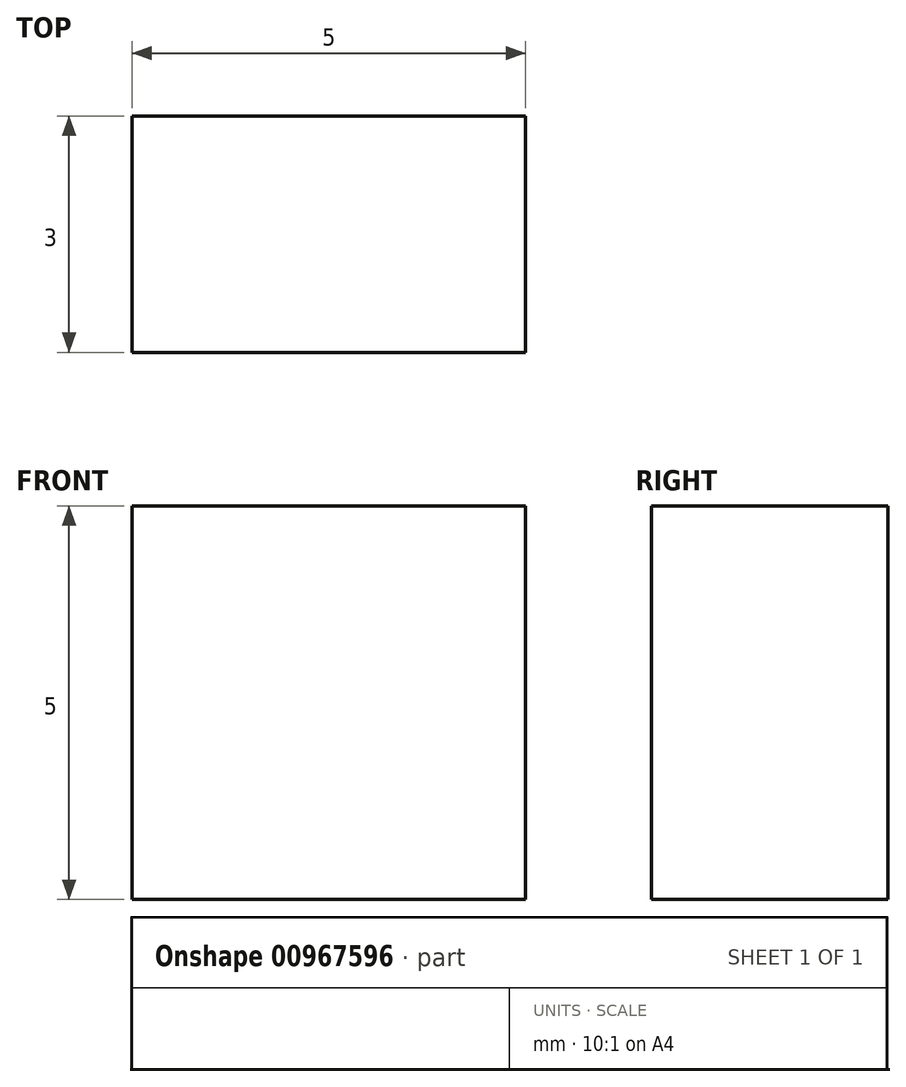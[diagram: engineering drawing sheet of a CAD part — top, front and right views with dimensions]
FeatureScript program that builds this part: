
annotation { "Feature Type Name" : "Feature", "Feature Type Description" : "" }
export const myFeature = defineFeature(function(context is Context, id is Id, definition is map)
    precondition{}
    {
        {
            var Q0;
            Q0=qCreatedBy(makeId("Front.planeOp"),FACE);
            var sketch = newSketch(context, id + "F0", { "sketchPlane" : qUnion([Q0])});
            skLineSegment(sketch, "E0.bottom", {"start": v(37.5, -50) * mm, "end": v(-37.5, -50) * mm});
            skLineSegment(sketch, "E0.top", {"start": v(37.5, 50) * mm, "end": v(-37.5, 50) * mm});
            skLineSegment(sketch, "E0.left", {"start": v(37.5, -50) * mm, "end": v(37.5, 50) * mm});
            skLineSegment(sketch, "E0.right", {"start": v(-37.5, -50) * mm, "end": v(-37.5, 50) * mm});
            skPoint(sketch, "E0.middle", {"position": v(0, 0) * mm});
            skLineSegment(sketch, "E1.0", {"start": v(47.5, 60) * mm, "end": v(-47.5, 60) * mm});
            skLineSegment(sketch, "E1.1", {"start": v(47.5, -60) * mm, "end": v(47.5, 60) * mm});
            skLineSegment(sketch, "E1.2", {"start": v(47.5, -60) * mm, "end": v(-47.5, -60) * mm});
            skLineSegment(sketch, "E1.3", {"start": v(-47.5, -60) * mm, "end": v(-47.5, 60) * mm});
            skLineSegment(sketch, "E2.bottom", {"start": v(-2.5, -50) * mm, "end": v(2.5, -50) * mm});
            skLineSegment(sketch, "E2.top", {"start": v(-2.5, 50) * mm, "end": v(2.5, 50) * mm});
            skLineSegment(sketch, "E2.left", {"start": v(-2.5, -50) * mm, "end": v(-2.5, 50) * mm});
            skLineSegment(sketch, "E2.right", {"start": v(2.5, -50) * mm, "end": v(2.5, 50) * mm});
            skLineSegment(sketch, "E3.bottom", {"start": v(37.5, -2.5) * mm, "end": v(-37.5, -2.5) * mm});
            skLineSegment(sketch, "E3.top", {"start": v(37.5, 2.5) * mm, "end": v(-37.5, 2.5) * mm});
            skLineSegment(sketch, "E3.left", {"start": v(37.5, -2.5) * mm, "end": v(37.5, 2.5) * mm});
            skLineSegment(sketch, "E3.right", {"start": v(-37.5, -2.5) * mm, "end": v(-37.5, 2.5) * mm});
            skSolve(sketch);
        }
        {
            var Q0;
            Q0=makeQuery(id+"F0.imprint","IMPRINT",FACE,{"disambiguationData":[TD([[makeQuery(id+"F0.imprint","IMPRINT",EDGE,{"derivedFrom":sQuery(id+"F0.wireOp",EDGE,"E1.0")}),1.0]])]});
            var Q1;
            {var subQ0=sQuery(id+"F0.wireOp",EDGE,"E2.top");Q1=makeQuery(id+"F0.imprint","IMPRINT",FACE,{"disambiguationData":[TD([[makeQuery(id+"F0.imprint","IMPRINT",EDGE,{"derivedFrom":subQ0}),-1.0]])]});}
            var Q2;
            {var subQ0=sQuery(id+"F0.wireOp",EDGE,"E2.bottom");Q2=makeQuery(id+"F0.imprint","IMPRINT",FACE,{"disambiguationData":[TD([[makeQuery(id+"F0.imprint","IMPRINT",EDGE,{"derivedFrom":subQ0}),1.0]])]});}
            var Q3;
            {var subQ5=sQuery(id+"F0.wireOp",EDGE,"E3.left");Q3=makeQuery(id+"F0.imprint","IMPRINT",FACE,{"disambiguationData":[TD([[makeQuery(id+"F0.imprint","IMPRINT",EDGE,{"derivedFrom":subQ5}),1.0]])]});}
            var Q4;
            {var subQ0=sQuery(id+"F0.wireOp",EDGE,"E3.bottom");var subQ1=sQuery(id+"F0.wireOp",EDGE,"E2.left");var subQ2=makeQuery(id+"F0.imprint","INTERSECT",VERTEX,{"derivedFrom":[subQ1,subQ0]});Q4=makeQuery(id+"F0.imprint","IMPRINT",FACE,{"disambiguationData":[TD([[makeQuery(id+"F0.imprint","IMPRINT",EDGE,{"disambiguationData":[TD([[subQ2,-1.0]])],"derivedFrom":subQ1}),-1.0]])]});}
            var Q5;
            {var subQ5=sQuery(id+"F0.wireOp",EDGE,"E3.right");Q5=makeQuery(id+"F0.imprint","IMPRINT",FACE,{"disambiguationData":[TD([[makeQuery(id+"F0.imprint","IMPRINT",EDGE,{"derivedFrom":subQ5}),-1.0]])]});}
            extrude(context, id + "F1", {"entities" : qUnion([Q0, Q1, Q2, Q3, Q4, Q5]), "depth" : 3 * mm, "offsetDistance" : 25 * mm});
        }
    });
